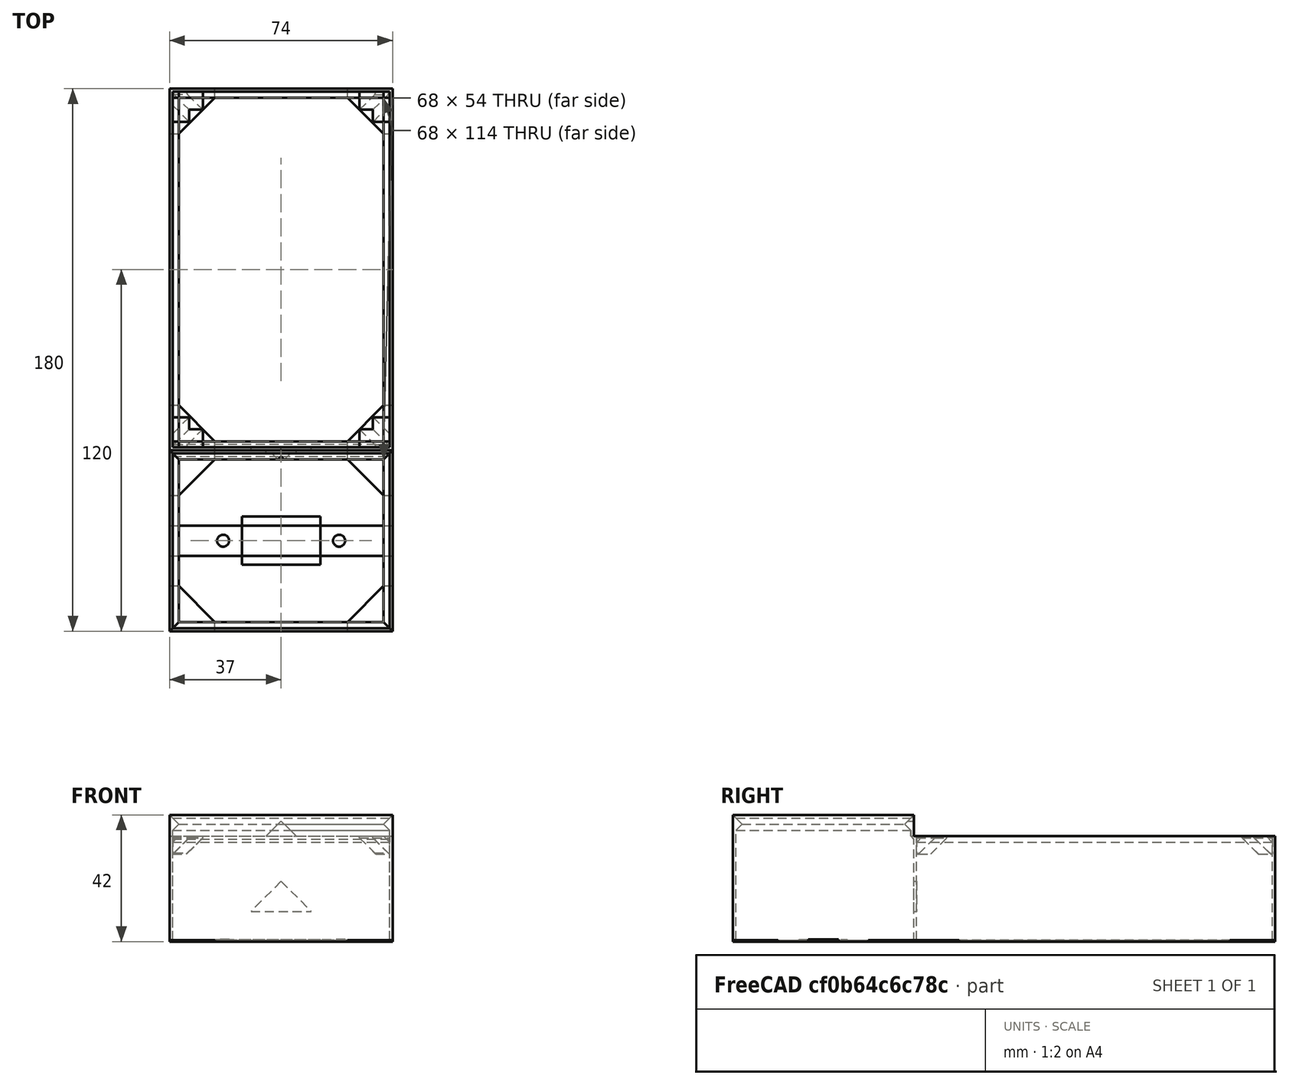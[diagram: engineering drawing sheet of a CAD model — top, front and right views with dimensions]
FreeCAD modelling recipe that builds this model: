
FCSTD DOCUMENT  (FreeCAD 0.16R)
Label: sonoff-T1-US-aufputz-v2-2-und-Steckdose_v1-1
License: All rights reserved
LicenseURL: http://en.wikipedia.org/wiki/All_rights_reserved
objects: Part::Box×37, Part::Chamfer×26, Part::Cut×14, Part::Fuse×5, Part::Cylinder×2
note: 84 computed .brp shape members not serialized (recipe doc carries the construction recipe); baked Part::Feature solids carry a one-line shape summary decoded from their .brp

FEATURE [Part::Box] Box  label="Basis"
  Height = 35
  Length = 74
  Width = 120
FEATURE [Part::Box] Box001  label="Ausschnitt"
  Height = 35
  Length = 72
  Placement = pos=(1,1,0) rot=(0,0,1;0rad)
  Width = 118
FEATURE [Part::Cut] Cut  label="Schaltergehäuse"
  Base = -> Box
  Tool = -> Box001
FEATURE [Part::Box] Box016  label="Cube012"
  Height = 0.5
  Length = 15
  Width = 15
FEATURE [Part::Box] Box017  label="Cube013"
  Height = 0.5
  Length = 15
  Placement = pos=(59,0,0) rot=(0,0,1;0rad)
  Width = 15
FEATURE [Part::Box] Box018  label="Cube014"
  Height = 0.5
  Length = 15
  Placement = pos=(59,105,0) rot=(0,0,1;0rad)
  Width = 15
FEATURE [Part::Box] Box019  label="Cube015"
  Height = 0.5
  Length = 15
  Placement = pos=(0,105,0) rot=(0,0,1;0rad)
  Width = 15
FEATURE [Part::Box] Box015  label="Basis002"
  Height = 0.5
  Length = 68
  Placement = pos=(3,3,0) rot=(0,0,1;0rad)
  Width = 114
FEATURE [Part::Box] Box014  label="Basis001"
  Height = 0.5
  Length = 74
  Width = 120
FEATURE [Part::Cut] Cut009  label="Schaltergehäuse Boden"
  Base = -> Box014
  Tool = -> Box015
FEATURE [Part::Chamfer] Chamfer
  Base = -> Box019
  Edges = 1 edges r=12: [Edge5]
FEATURE [Part::Chamfer] Chamfer001
  Base = -> Box018
  Edges = 1 edges r=12: [Edge1]
FEATURE [Part::Chamfer] Chamfer002
  Base = -> Box017
  Edges = 1 edges r=12: [Edge3]
  Placement = pos=(0,-60,0) rot=(0,0,1;0rad)
FEATURE [Part::Chamfer] Chamfer003
  Base = -> Box016
  Edges = 1 edges r=12: [Edge7]
  Placement = pos=(0,-60,0) rot=(0,0,1;0rad)
FEATURE [Part::Box] Box020  label="Cube"
  Height = 6
  Length = 4.5
  Placement = pos=(6.5,7,29) rot=(0,0,1;0rad)
  Width = 4
FEATURE [Part::Box] Box021  label="Cube016"
  Height = 6
  Length = 10
  Placement = pos=(1,1,29) rot=(0,0,1;0rad)
  Width = 10
FEATURE [Part::Box] Box022  label="Cube017"
  Height = 6
  Length = 4.5
  Placement = pos=(63,7,29) rot=(0,0,1;0rad)
  Width = 4
FEATURE [Part::Box] Box023  label="Cube018"
  Height = 6
  Length = 10
  Placement = pos=(63,1,29) rot=(0,0,1;0rad)
  Width = 10
FEATURE [Part::Box] Box024  label="Cube019"
  Height = 6
  Length = 4.5
  Placement = pos=(63,109,29) rot=(0,0,1;0rad)
  Width = 4
FEATURE [Part::Box] Box025  label="Cube020"
  Height = 6
  Length = 10
  Placement = pos=(63,109,29) rot=(0,0,1;0rad)
  Width = 10
FEATURE [Part::Box] Box026  label="Cube021"
  Height = 6
  Length = 4.5
  Placement = pos=(6.5,109,29) rot=(0,0,1;0rad)
  Width = 4
FEATURE [Part::Box] Box027  label="Cube022"
  Height = 6
  Length = 10
  Placement = pos=(1,109,29) rot=(0,0,1;0rad)
  Width = 10
FEATURE [Part::Box] Box028  label="Cube023"
  Height = 2
  Length = 72
  Placement = pos=(1,1,33) rot=(0,0,1;0rad)
  Width = 2
FEATURE [Part::Box] Box029  label="Cube024"
  Height = 2
  Length = 2
  Placement = pos=(1,1,33) rot=(0,0,1;0rad)
  Width = 118
FEATURE [Part::Box] Box030  label="Cube025"
  Height = 2
  Length = 72
  Placement = pos=(1,117,33) rot=(0,0,1;0rad)
  Width = 2
FEATURE [Part::Box] Box031  label="Cube026"
  Height = 2
  Length = 2
  Placement = pos=(71,1,33) rot=(0,0,1;0rad)
  Width = 118
FEATURE [Part::Chamfer] Chamfer008
  Base = -> Box029
  Edges = 1 edges r=1.99: [Edge8]
FEATURE [Part::Chamfer] Chamfer009
  Base = -> Box028
  Edges = 1 edges r=1.99: [Edge11]
FEATURE [Part::Chamfer] Chamfer010
  Base = -> Box031
  Edges = 1 edges r=1.99: [Edge4]
FEATURE [Part::Chamfer] Chamfer011
  Base = -> Box030
  Edges = 1 edges r=1.99: [Edge9]
FEATURE [Part::Cut] Cut010
  Base = -> Box027
  Tool = -> Box026
FEATURE [Part::Cut] Cut011
  Base = -> Box025
  Tool = -> Box024
FEATURE [Part::Cut] Cut012
  Base = -> Box021
  Tool = -> Box020
FEATURE [Part::Cut] Cut013
  Base = -> Box023
  Tool = -> Box022
FEATURE [Part::Chamfer] Chamfer012
  Base = -> Cut010
  Edges = 4 edges r=5.49: [Edge5,Edge14,Edge15,Edge16]
FEATURE [Part::Chamfer] Chamfer013
  Base = -> Chamfer012
  Edges = 1 edges r=0.5: [Edge17]
FEATURE [Part::Chamfer] Chamfer014
  Base = -> Cut012
  Edges = 4 edges r=5.4: [Edge12,Edge14,Edge15,Edge16]
FEATURE [Part::Chamfer] Chamfer015
  Base = -> Cut013
  Edges = 4 edges r=5.4: [Edge3,Edge10,Edge12,Edge13]
FEATURE [Part::Chamfer] Chamfer016
  Base = -> Cut011
  Edges = 4 edges r=5.4: [Edge4,Edge5,Edge15,Edge16]
FEATURE [Part::Chamfer] Chamfer017
  Base = -> Chamfer016
  Edges = 1 edges r=0.5: [Edge19]
FEATURE [Part::Chamfer] Chamfer018
  Base = -> Chamfer014
  Edges = 1 edges r=0.5: [Edge17]
FEATURE [Part::Chamfer] Chamfer019
  Base = -> Chamfer015
  Edges = 1 edges r=0.5: [Edge19]
FEATURE [Part::Box] Box032  label="Basis Stecker"
  Height = 42
  Length = 74
  Placement = pos=(0,-60,0) rot=(0,0,1;0rad)
  Width = 60
FEATURE [Part::Box] Box033  label="Ausschnitt Stecker"
  Height = 42
  Length = 72
  Placement = pos=(1,-59,0) rot=(0,0,1;0rad)
  Width = 58
FEATURE [Part::Cut] Cut014
  Base = -> Box032
  Tool = -> Box033
FEATURE [Part::Box] Box034  label="Boden Stecker"
  Height = 0.5
  Length = 74
  Placement = pos=(0,-60,0) rot=(0,0,1;0rad)
  Width = 60
FEATURE [Part::Box] Box035  label="Boden Ausschnitt Stecker"
  Height = 0.5
  Length = 68
  Placement = pos=(3,-57,0) rot=(0,0,1;0rad)
  Width = 54
FEATURE [Part::Cut] Cut015  label="Steckergehäuse Boden"
  Base = -> Box034
  Tool = -> Box035
FEATURE [Part::Chamfer] Chamfer020  label="Steckergehäuse"
  Base = -> Cut014
  Edges = 4 edges r=0.99: [Edge10,Edge11,Edge12,Edge13]
FEATURE [Part::Box] Box036  label="Cube027"
  Height = 0.7
  Length = 74
  Placement = pos=(0,-35,0) rot=(0,0,1;0rad)
  Width = 10
FEATURE [Part::Box] Box037  label="Cube028"
  Height = 0.7
  Length = 26
  Placement = pos=(24,-38,0) rot=(0,0,1;0rad)
  Width = 16
FEATURE [Part::Cylinder] Cylinder
  Angle = 360
  Height = 10
  Placement = pos=(17.75,-30,0) rot=(0,0,1;0rad)
  Radius = 2
FEATURE [Part::Cylinder] Cylinder001
  Angle = 360
  Height = 10
  Placement = pos=(56.25,-30,0) rot=(0,0,1;0rad)
  Radius = 2
FEATURE [Part::Cut] Cut016
  Base = -> Box036
  Tool = -> Cylinder
FEATURE [Part::Cut] Cut017
  Base = -> Cut016
  Tool = -> Cylinder001
FEATURE [Part::Fuse] Fusion
  Base = -> Cut
  Tool = -> Cut009
FEATURE [Part::Fuse] Fusion001
  Base = -> Fusion
  Tool = -> Cut015
FEATURE [Part::Fuse] Fusion002
  Base = -> Fusion001
  Tool = -> Chamfer020
FEATURE [Part::Box] Box038  label="Kragen Stecker"
  Height = 4.1
  Length = 74
  Placement = pos=(0,-60,0) rot=(0,0,1;0rad)
  Width = 60
FEATURE [Part::Box] Box039  label="Kragen Stecker Ausschnitt"
  Height = 4.1
  Length = 68
  Placement = pos=(3,-57,0) rot=(0,0,1;0rad)
  Width = 54
FEATURE [Part::Cut] Cut019
  Base = -> Box038
  Placement = pos=(0,0,36.9) rot=(0,0,1;0rad)
  Tool = -> Box039
FEATURE [Part::Chamfer] Chamfer021
  Base = -> Cut019
  Edges = 4 edges r=2: [Edge10,Edge11,Edge12,Edge13]
FEATURE [Part::Chamfer] Chamfer022  label="Kragen"
  Base = -> Chamfer021
  Edges = 4 edges r=2: [Edge26,Edge29,Edge31,Edge32]
FEATURE [Part::Box] Box040  label="Cube029"
  Height = 0.5
  Length = 15
  Placement = pos=(59,105,0) rot=(0,0,1;0rad)
  Width = 15
FEATURE [Part::Chamfer] Chamfer023
  Base = -> Box040
  Edges = 1 edges r=12: [Edge1]
  Placement = pos=(0,-120,0) rot=(0,0,1;0rad)
FEATURE [Part::Box] Box041  label="Cube030"
  Height = 0.5
  Length = 15
  Placement = pos=(0,105,0) rot=(0,0,1;0rad)
  Width = 15
FEATURE [Part::Chamfer] Chamfer024
  Base = -> Box041
  Edges = 1 edges r=12: [Edge5]
  Placement = pos=(0,-120,0) rot=(0,0,1;0rad)
FEATURE [Part::Box] Box042  label="Cube031"
  Height = 0.5
  Length = 15
  Placement = pos=(59,0,0) rot=(0,0,1;0rad)
  Width = 15
FEATURE [Part::Chamfer] Chamfer025
  Base = -> Box042
  Edges = 1 edges r=12: [Edge3]
FEATURE [Part::Box] Box043  label="Cube032"
  Height = 0.5
  Length = 15
  Width = 15
FEATURE [Part::Chamfer] Chamfer026
  Base = -> Box043
  Edges = 1 edges r=12: [Edge7]
FEATURE [Part::Box] Box044  label="Cube033"
  Height = 37
  Length = 72
  Placement = pos=(1,-1,0) rot=(0,0,1;0rad)
  Width = 1
FEATURE [Part::Cut] Cut020  label="Gehäuse"
  Base = -> Fusion002
  Tool = -> Box044
FEATURE [Part::Box] Box045  label="Cube034"
  Height = 4
  Length = 72
  Placement = pos=(1,-1,34) rot=(0,0,1;0rad)
  Width = 1
FEATURE [Part::Chamfer] Chamfer027  label="Verstärkung"
  Base = -> Box045
  Edges = 1 edges r=0.99: [Edge9]
FEATURE [Part::Box] Box046  label="Cube035"
  Height = 5
  Length = 10
  Placement = pos=(32,-5,35) rot=(0,0,1;0rad)
  Width = 10
FEATURE [Part::Chamfer] Chamfer028
  Base = -> Box046
  Edges = 2 edges r=4.99: [Edge2,Edge6]
FEATURE [Part::Fuse] Fusion003
  Base = -> Chamfer022
  Tool = -> Cut020
FEATURE [Part::Fuse] Fusion004
  Base = -> Fusion003
  Tool = -> Chamfer027
FEATURE [Part::Cut] Cut021
  Base = -> Fusion004
  Tool = -> Chamfer028
FEATURE [Part::Box] Box047  label="Kabelloch000"
  Height = 10
  Length = 20
  Placement = pos=(27,0,10) rot=(0,0,1;0rad)
  Width = 10
FEATURE [Part::Chamfer] Chamfer029
  Base = -> Box047
  Edges = 2 edges r=9.99: [Edge2,Edge6]
FEATURE [Part::Cut] Cut022
  Base = -> Cut021
  Tool = -> Chamfer029
FEATURE [Part::Box] Box048  label="Cube036"
  Height = 0.5
  Length = 72
  Placement = pos=(1,-2,0) rot=(0,0,1;0rad)
  Width = 4
